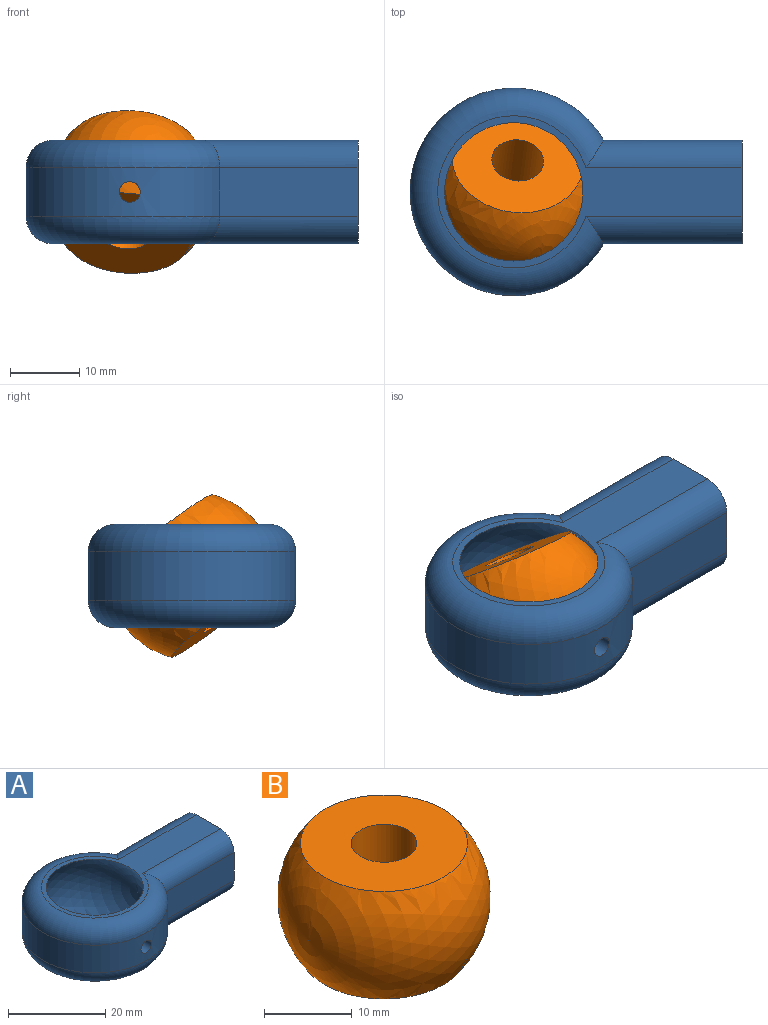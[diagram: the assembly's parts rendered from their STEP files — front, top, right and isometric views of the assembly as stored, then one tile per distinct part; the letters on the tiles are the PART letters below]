
ASSEMBLY  parts=2 mates=1
PART A: 16 faces, bbox 49.2x32.5x25 mm
  f0: cylinder r=15mm len=30mm, axis (0,0,-1), area 542.7mm2, adj f2,f4,f11,f13,f15
  f1: sphere r=12.5mm, area 1171mm2, adj f5,f6,f15
  f2: plane 20x7mm, normal (0,-1,0), area 140mm2, adj f0,f3,f10,f12
  f3: plane 15x15mm, normal (1,0,0), area 161mm2, adj f2,f4,f5,f6,f7,f9,f10,f12
  f4: plane 20x7mm, normal (0,1,0), area 140mm2, adj f0,f3,f9,f14
  f5: plane 43.99x22mm, normal (0,0,1), area 221.2mm2, adj f1,f3,f12,f13,f14
  f6: plane 43.99x22mm, normal (0,0,-1), area 221.2mm2, adj f1,f3,f9,f10,f11
  f7: cylinder r=4mm len=15mm, axis (1,0,0), area 377mm2, adj f3,f8
  f8: plane 8x8mm, normal (1,0,0), area 50.3mm2, adj f7
  f9: cylinder r=4mm len=22.56mm, axis (-1,0,0), area 131.3mm2, adj f3,f4,f6,f11
  f10: cylinder r=4mm len=22.56mm, axis (1,0,0), area 131.3mm2, adj f2,f3,f6,f11
  f11: torus R=11mm, axis (0,0,1), area 455.9mm2, adj f0,f6,f9,f10
  f12: cylinder r=4mm len=22.56mm, axis (-1,0,0), area 131.3mm2, adj f2,f3,f5,f13
  f13: torus R=11mm, axis (0,0,1), area 455.9mm2, adj f0,f5,f12,f14
  f14: cylinder r=4mm len=22.56mm, axis (1,0,0), area 131.3mm2, adj f3,f4,f5,f13
  f15: cylinder r=1.5mm len=3mm, axis (0,1,0), area 24.1mm2, adj f0,f1
PART B: 4 faces, bbox 24.3x24.3x24.3 mm
  f0: plane 19.05x19.05mm, normal (0,0,1), area 241mm2, adj f1,f3
  f1: cylinder r=3.75mm len=15mm, axis (0,0,-1), area 353.4mm2, adj f0,f2
  f2: plane 19.05x19.05mm, normal (0,0,-1), area 241mm2, adj f1,f3
  f3: sphere r=12.12mm, area 1142.7mm2, adj f0,f2
PLACE A t=(25.71,7.9,10.66)mm fixed
PLACE B rot(axis=(-0.19,0.34,0.92),112.5deg) t=(-18.86,28.54,-6.02)mm
MATE ball A.f0 <-> B.f1  axis (0,0,1) through (-7.28,7.9,18.16)mm
